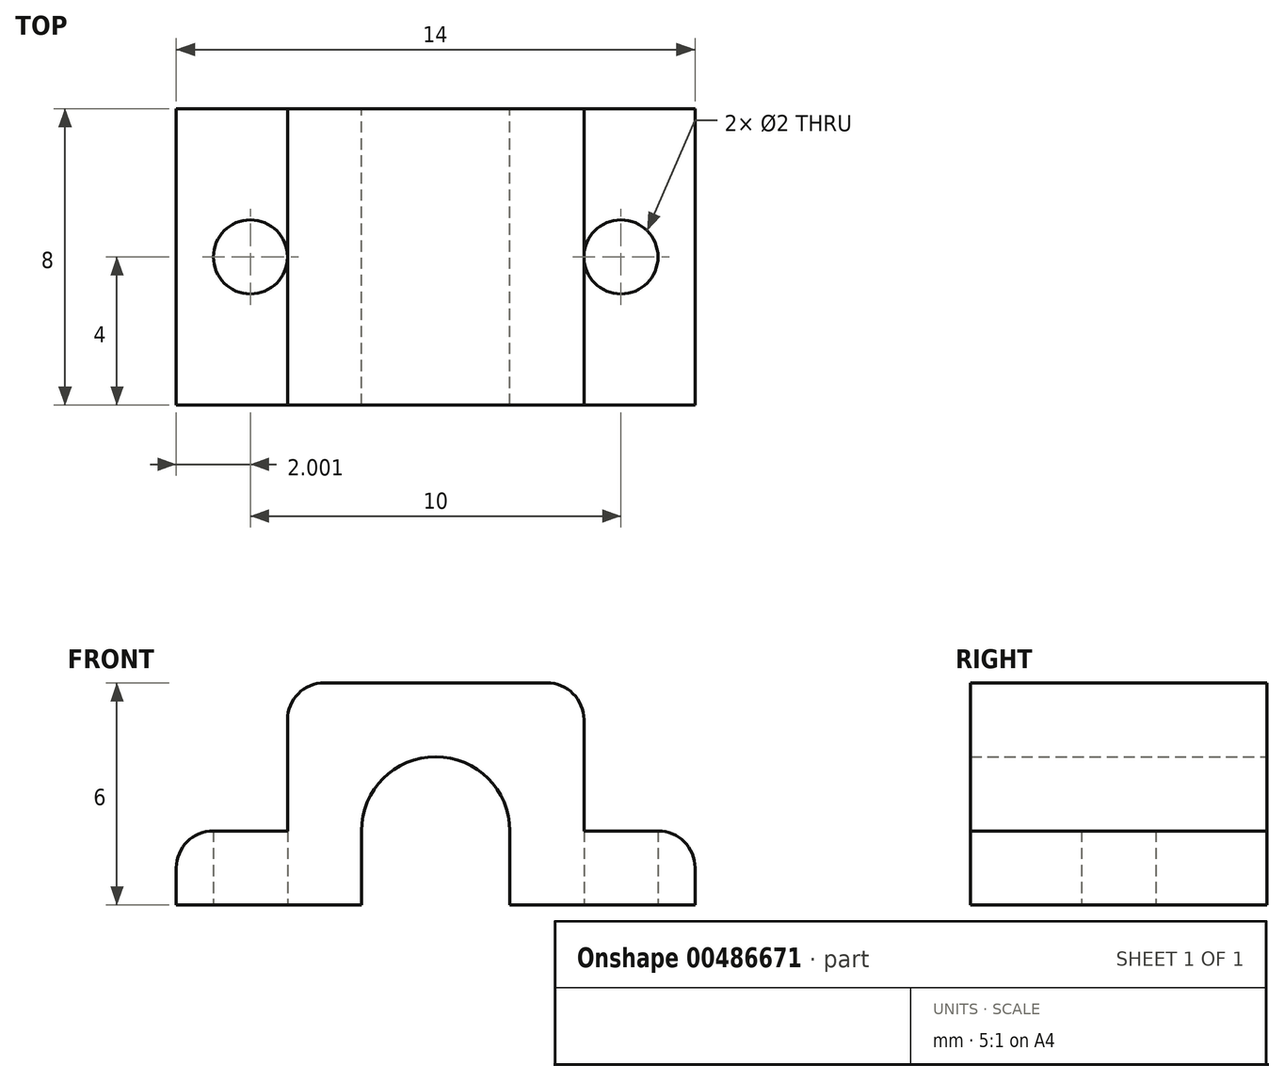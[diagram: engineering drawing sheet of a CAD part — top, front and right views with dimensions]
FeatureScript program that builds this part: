
annotation { "Feature Type Name" : "Feature", "Feature Type Description" : "" }
export const myFeature = defineFeature(function(context is Context, id is Id, definition is map)
    precondition{}
    {
        {
            var Q0;
            Q0=qCreatedBy(makeId("Front.planeOp"),FACE);
            var sketch = newSketch(context, id + "F0", { "sketchPlane" : qUnion([Q0])});
            skLineSegment(sketch, "E0", {"start": v(-10.1, 0) * mm, "end": v(-10.1, 2) * mm});
            skLineSegment(sketch, "E1", {"start": v(-10.1, 2) * mm, "end": v(-7.1, 2) * mm});
            skLineSegment(sketch, "E2", {"start": v(-7.1, 2) * mm, "end": v(-7.1, 6) * mm});
            skLineSegment(sketch, "E3", {"start": v(-7.1, 6) * mm, "end": v(0.9, 6) * mm});
            skLineSegment(sketch, "E4", {"start": v(0.9, 6) * mm, "end": v(0.9, 2) * mm});
            skLineSegment(sketch, "E5", {"start": v(0.9, 2) * mm, "end": v(3.9, 2) * mm});
            skLineSegment(sketch, "E6", {"start": v(3.9, 2) * mm, "end": v(3.9, 0) * mm});
            skLineSegment(sketch, "E7", {"start": v(3.9, 0) * mm, "end": v(-1.1, 0) * mm});
            skLineSegment(sketch, "E8", {"start": v(-1.1, 0) * mm, "end": v(-1.1, 2) * mm});
            skLineSegment(sketch, "E9", {"start": v(-3.1, 4) * mm, "end": v(-3.1, 4) * mm});
            skLineSegment(sketch, "E10", {"start": v(-5.1, 2) * mm, "end": v(-5.1, 0) * mm});
            skLineSegment(sketch, "E11", {"start": v(-5.1, 0) * mm, "end": v(-10.1, 0) * mm});
            skPoint(sketch, "E12.visualSharp", {"position": v(-5.1, 4) * mm});
            skArc(sketch, "E12.filletArc", {"start": v(-3.1, 4) * mm, "mid": v(-4.52, 3.41) * mm, "end": v(-5.1, 2) * mm});
            skPoint(sketch, "E13.visualSharp", {"position": v(-1.1, 4) * mm});
            skArc(sketch, "E13.filletArc", {"start": v(-1.1, 2) * mm, "mid": v(-1.7, 3.41) * mm, "end": v(-3.1, 4) * mm});
            skSolve(sketch);
        }
        {
            var Q0;
            Q0=makeQuery(id+"F0.imprint","IMPRINT",FACE,{"disambiguationData":[TD([[makeQuery(id+"F0.imprint","IMPRINT",EDGE,{"derivedFrom":sQuery(id+"F0.wireOp",EDGE,"E0")}),-1.0]])]});
            extrude(context, id + "F1", {"entities" : qUnion([Q0]), "depth" : 8 * mm});
        }
        {
            var Q0;
            Q0=makeQuery(id+"F1.opExtrude","SWEPT_FACE",FACE,{"disambiguationData":[OSD([sQuery(id+"F0.wireOp",EDGE,"E11")])]});
            var sketch = newSketch(context, id + "F2", { "sketchPlane" : qUnion([Q0])});
            skCircle(sketch, "E14", {"center": v(-8.1, 4) * mm, "radius": 1 * mm});
            skSolve(sketch);
        }
        {
            var Q0;
            Q0=makeQuery(id+"F2.imprint","IMPRINT",FACE,{"disambiguationData":[TD([[makeQuery(id+"F2.imprint","IMPRINT",EDGE,{"derivedFrom":sQuery(id+"F2.wireOp",EDGE,"E14")}),1.0]])]});
            extrude(context, id + "F3", {"entities" : qUnion([Q0]), "operationType" : NewBodyOperationType.REMOVE, "oppositeDirection" : true, "depth" : 2 * mm});
        }
        {
            var Q0;
            Q0=makeQuery(id+"F1.opExtrude","SWEPT_FACE",FACE,{"disambiguationData":[OSD([sQuery(id+"F0.wireOp",EDGE,"E7")])]});
            var sketch = newSketch(context, id + "F4", { "sketchPlane" : qUnion([Q0])});
            skCircle(sketch, "E15", {"center": v(1.9, 4) * mm, "radius": 1 * mm});
            skSolve(sketch);
        }
        {
            var Q0;
            Q0=makeQuery(id+"F4.imprint","IMPRINT",FACE,{"disambiguationData":[TD([[makeQuery(id+"F4.imprint","IMPRINT",EDGE,{"derivedFrom":sQuery(id+"F4.wireOp",EDGE,"E15")}),1.0]])]});
            extrude(context, id + "F5", {"entities" : qUnion([Q0]), "operationType" : NewBodyOperationType.REMOVE, "oppositeDirection" : true, "depth" : 2 * mm});
        }
        {
            var Q0;
            Q0=makeQuery(id+"F1.opExtrude","SWEPT_EDGE",EDGE,{"disambiguationData":[OSD([sQuery(id+"F0.wireOp",EDGE,"E0"),sQuery(id+"F0.wireOp",EDGE,"E1")])]});
            var Q1;
            Q1=makeQuery(id+"F1.opExtrude","SWEPT_EDGE",EDGE,{"disambiguationData":[OSD([sQuery(id+"F0.wireOp",EDGE,"E2"),sQuery(id+"F0.wireOp",EDGE,"E3")])]});
            var Q2;
            Q2=makeQuery(id+"F1.opExtrude","SWEPT_EDGE",EDGE,{"disambiguationData":[OSD([sQuery(id+"F0.wireOp",EDGE,"E3"),sQuery(id+"F0.wireOp",EDGE,"E4")])]});
            var Q3;
            Q3=makeQuery(id+"F1.opExtrude","SWEPT_EDGE",EDGE,{"disambiguationData":[OSD([sQuery(id+"F0.wireOp",EDGE,"E5"),sQuery(id+"F0.wireOp",EDGE,"E6")])]});
            fillet(context, id + "F6", {"entities" : qUnion([Q0, Q1, Q2, Q3]), "radius" : 1 * mm, "tangentPropagation" : true, "allowEdgeOverflow" : false});
        }
    });
